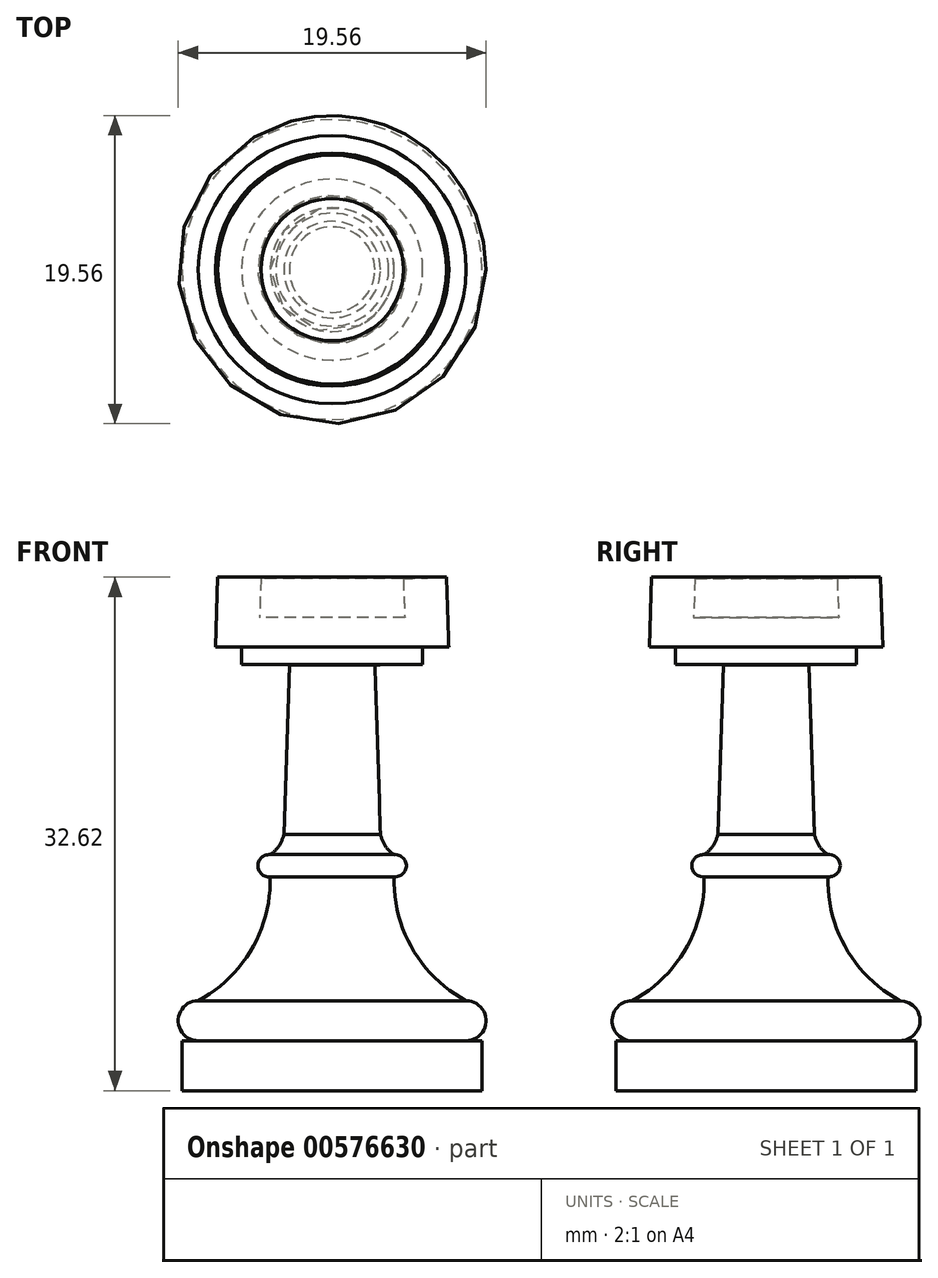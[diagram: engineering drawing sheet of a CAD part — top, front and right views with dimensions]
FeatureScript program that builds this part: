
annotation { "Feature Type Name" : "Feature", "Feature Type Description" : "" }
export const myFeature = defineFeature(function(context is Context, id is Id, definition is map)
    precondition{}
    {
        {
            var Q0;
            Q0=qCreatedBy(makeId("Front.planeOp"),FACE);
            var sketch = newSketch(context, id + "F0", { "sketchPlane" : qUnion([Q0])});
            skLineSegment(sketch, "E0", {"start": v(0, 0) * mm, "end": v(9.53, 0) * mm});
            skLineSegment(sketch, "E1", {"start": v(9.53, 0) * mm, "end": v(9.53, 3.18) * mm});
            skLineSegment(sketch, "E2.bottom", {"start": v(9.53, 3.18) * mm, "end": v(8.5, 3.18) * mm});
            skLineSegment(sketch, "E2.top", {"start": v(9.53, 3.18) * mm, "end": v(8.5, 3.18) * mm});
            skLineSegment(sketch, "E2.left", {"start": v(9.53, 3.18) * mm, "end": v(9.53, 3.18) * mm});
            skLineSegment(sketch, "E2.right", {"start": v(8.5, 3.18) * mm, "end": v(8.5, 3.18) * mm});
            skArc(sketch, "E3", {"start": v(8.5, 3.18) * mm, "mid": v(9.78, 4.45) * mm, "end": v(8.5, 5.72) * mm});
            skArc(sketch, "E4", {"start": v(3.94, 13.59) * mm, "mid": v(5.1, 9) * mm, "end": v(8.5, 5.72) * mm});
            skArc(sketch, "E5", {"start": v(3.94, 13.59) * mm, "mid": v(4.71, 14.29) * mm, "end": v(3.94, 14.99) * mm});
            skArc(sketch, "E6", {"start": v(3.07, 16.28) * mm, "mid": v(3.38, 15.55) * mm, "end": v(3.94, 14.99) * mm});
            skLineSegment(sketch, "E7", {"start": v(3.07, 16.28) * mm, "end": v(2.72, 27.04) * mm});
            skLineSegment(sketch, "E8", {"start": v(2.72, 27.04) * mm, "end": v(3.59, 27.07) * mm});
            skLineSegment(sketch, "E9", {"start": v(3.59, 27.07) * mm, "end": v(5.75, 27.07) * mm});
            skLineSegment(sketch, "E10", {"start": v(5.75, 27.07) * mm, "end": v(5.75, 28.18) * mm});
            skLineSegment(sketch, "E11", {"start": v(5.75, 28.18) * mm, "end": v(7.4, 28.18) * mm});
            skLineSegment(sketch, "E12", {"start": v(4.61, 30.04) * mm, "end": v(0, 30.04) * mm});
            skLineSegment(sketch, "E13", {"start": v(0, 30.04) * mm, "end": v(0, 0) * mm});
            skLineSegment(sketch, "E14", {"start": v(7.4, 28.18) * mm, "end": v(7.26, 32.62) * mm});
            skLineSegment(sketch, "E15", {"start": v(7.26, 32.62) * mm, "end": v(4.52, 32.53) * mm});
            skLineSegment(sketch, "E16", {"start": v(4.52, 32.53) * mm, "end": v(4.61, 30.04) * mm});
            skSolve(sketch);
        }
        {
            var Q0;
            Q0=makeQuery(id+"F0.imprint","IMPRINT",FACE,{"disambiguationData":[TD([[makeQuery(id+"F0.imprint","IMPRINT",EDGE,{"derivedFrom":sQuery(id+"F0.wireOp",EDGE,"E0")}),1.0]])]});
            var Q1;
            Q1=sQuery(id+"F0.wireOp",EDGE,"E13");
            revolve(context, id + "F1", {"entities" : qUnion([Q0]), "axis" : qUnion([Q1]), "revolveType" : RevolveType.FULL});
        }
    });
